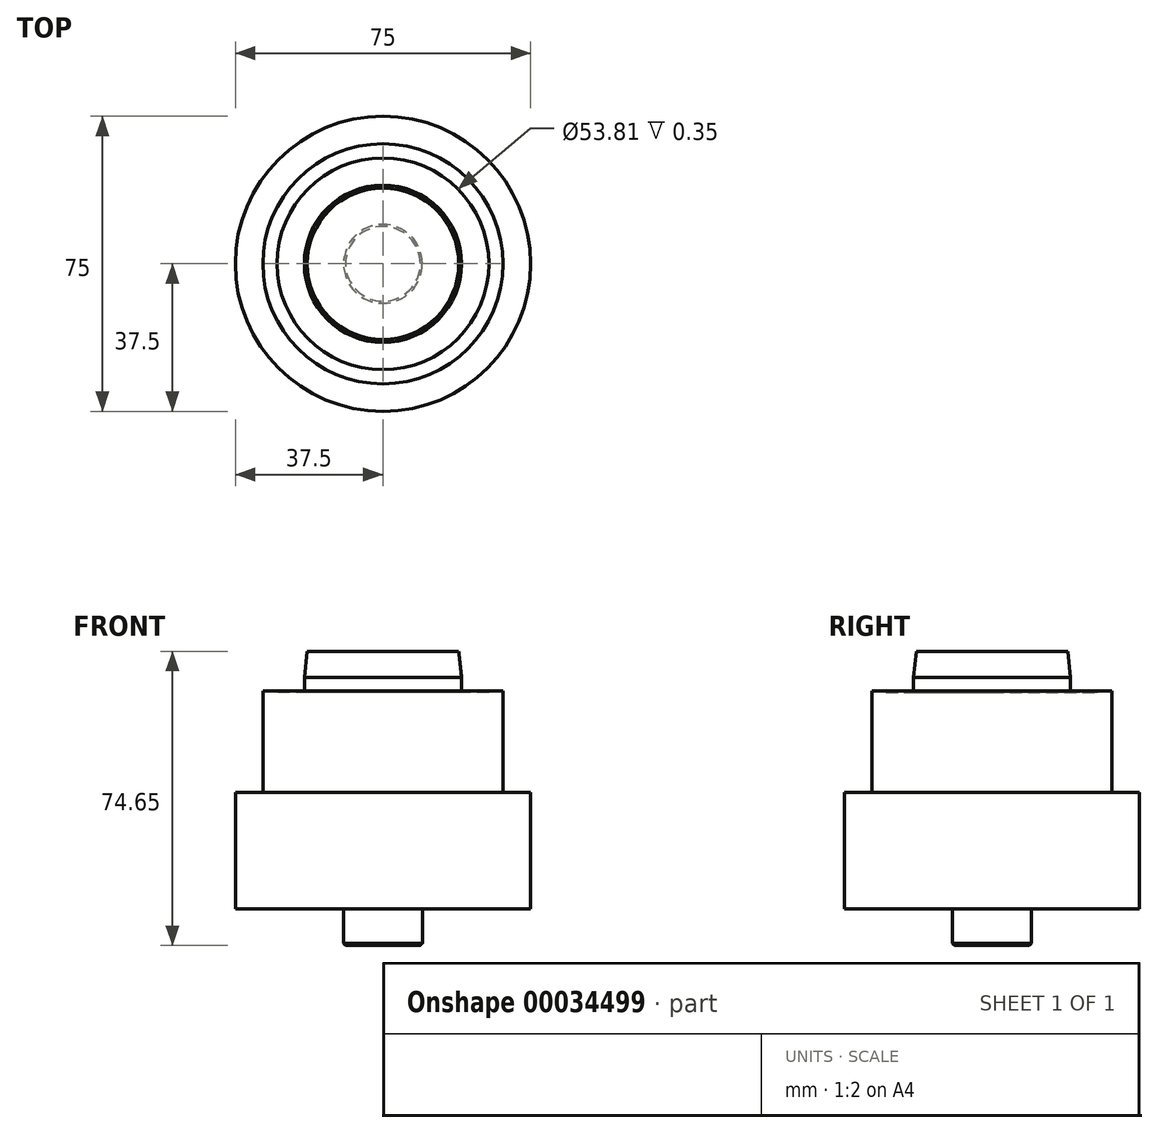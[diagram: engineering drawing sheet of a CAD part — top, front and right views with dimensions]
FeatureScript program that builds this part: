
annotation { "Feature Type Name" : "Feature", "Feature Type Description" : "" }
export const myFeature = defineFeature(function(context is Context, id is Id, definition is map)
    precondition{}
    {
        {
            var Q0;
            Q0=qCreatedBy(makeId("Front.planeOp"),FACE);
            var sketch = newSketch(context, id + "F0", { "sketchPlane" : qUnion([Q0])});
            skLineSegment(sketch, "E0", {"start": v(0, 93.75) * mm, "end": v(0, -3.98) * mm, "construction": true});
            skSolve(sketch);
        }
        {
            var Q0;
            Q0=qCreatedBy(makeId("Top.planeOp"),FACE);
            var sketch = newSketch(context, id + "F1", { "sketchPlane" : qUnion([Q0])});
            skCircle(sketch, "E1", {"center": v(0, 0) * mm, "radius": 10 * mm});
            skSolve(sketch);
        }
        {
            var Q0;
            Q0 = qSketchRegion(id + "F1", true);
            extrude(context, id + "F2", {"entities" : qUnion([Q0]), "depth" : 9.2 * mm});
        }
        {
            var Q0;
            Q0=makeQuery(id+"F2.opExtrude","CAP_FACE",FACE,{"disambiguationData":[OSD([sQuery(id+"F1.wireOp",EDGE,"E1")])],"isStart":false});
            var sketch = newSketch(context, id + "F3", { "sketchPlane" : qUnion([Q0])});
            skCircle(sketch, "E2", {"center": v(0, 0) * mm, "radius": 37.5 * mm});
            skSolve(sketch);
        }
        {
            var Q0;
            Q0 = qSketchRegion(id + "F3", true);
            extrude(context, id + "F4", {"entities" : qUnion([Q0]), "operationType" : NewBodyOperationType.ADD, "depth" : 29.6 * mm});
        }
        {
            var Q0;
            Q0=makeQuery(id+"F4.opExtrude","CAP_FACE",FACE,{"disambiguationData":[OSD([sQuery(id+"F3.wireOp",EDGE,"E2")])],"isStart":false});
            var sketch = newSketch(context, id + "F5", { "sketchPlane" : qUnion([Q0])});
            skCircle(sketch, "E3", {"center": v(0, 0) * mm, "radius": 30.5 * mm});
            skSolve(sketch);
        }
        {
            var Q0;
            Q0 = qSketchRegion(id + "F5", true);
            extrude(context, id + "F6", {"entities" : qUnion([Q0]), "operationType" : NewBodyOperationType.ADD, "depth" : 25.8 * mm});
        }
        {
            var Q0;
            Q0=makeQuery(id+"F6.opExtrude","CAP_FACE",FACE,{"disambiguationData":[OSD([sQuery(id+"F5.wireOp",EDGE,"E3")])],"isStart":false});
            var sketch = newSketch(context, id + "F7", { "sketchPlane" : qUnion([Q0])});
            skCircle(sketch, "E4", {"center": v(0, 0) * mm, "radius": 26.9 * mm});
            skSolve(sketch);
        }
        {
            var Q0;
            Q0 = qSketchRegion(id + "F7", true);
            extrude(context, id + "F8", {"entities" : qUnion([Q0]), "operationType" : NewBodyOperationType.REMOVE, "oppositeDirection" : true, "depth" : 0.35 * mm});
        }
        {
            var Q0;
            Q0=makeQuery(id+"F8.boolean.opBoolean","COPY",FACE,{"derivedFrom":makeQuery(id+"F8.opExtrude","CAP_FACE",FACE,{"disambiguationData":[OSD([sQuery(id+"F7.wireOp",EDGE,"E4")])],"isStart":false})});
            var sketch = newSketch(context, id + "F9", { "sketchPlane" : qUnion([Q0])});
            skLineSegment(sketch, "E5", {"start": v(0, 17.38) * mm, "end": v(0, -19.78) * mm, "construction": true});
            skSolve(sketch);
        }
        {
            var Q0;
            Q0=makeQuery(id+"F6UNSWDGwlZitm0_1.opRevolve","SWEPT_EDGE",EDGE,{"disambiguationData":[OSD([sQuery(id+"Fxo4OY0H7vpecpR_1.wireOp",EDGE,"9f0356d1-925e-4ddc-828d-e82d80c523e6.bottom"),sQuery(id+"Fxo4OY0H7vpecpR_1.wireOp",EDGE,"090784d4-c261-4ad9-9b5f-4208fe60787c")])]});
            var Q1;
            Q1=makeQuery(id+"F8.boolean.opBoolean","COPY",EDGE,{"derivedFrom":makeQuery(id+"F8.opExtrude","CAP_EDGE",EDGE,{"disambiguationData":[OSD([sQuery(id+"F7.wireOp",EDGE,"E4")])],"isStart":true})});
            var Q2;
            Q2=makeQuery(id+"F2.opExtrude","CAP_EDGE",EDGE,{"disambiguationData":[OSD([sQuery(id+"F1.wireOp",EDGE,"E1")])],"isStart":true});
            chamfer(context, id + "F10", {"entities" : qUnion([Q0, Q1, Q2]), "width" : 0.5 * mm, "tangentPropagation" : true});
        }
        {
            var Q0;
            Q0=qCreatedBy(makeId("Front.planeOp"),FACE);
            var sketch = newSketch(context, id + "F11", { "sketchPlane" : qUnion([Q0])});
            skLineSegment(sketch, "E6.bottom", {"start": v(0, 74.65) * mm, "end": v(-19.25, 74.65) * mm});
            skLineSegment(sketch, "E6.top", {"start": v(0, 64.25) * mm, "end": v(-19.98, 64.25) * mm});
            skLineSegment(sketch, "E6.left", {"start": v(0, 74.65) * mm, "end": v(0, 64.25) * mm});
            skLineSegment(sketch, "E6.right", {"start": v(-19.98, 68.05) * mm, "end": v(-19.98, 64.25) * mm});
            skLineSegment(sketch, "E7", {"start": v(-19.25, 74.65) * mm, "end": v(-19.98, 68.05) * mm});
            skSolve(sketch);
        }
        {
            var Q0;
            Q0 = qSketchRegion(id + "F11", true);
            var Q1;
            Q1=sQuery(id+"F0.wireOp",EDGE,"E0");
            revolve(context, id + "F12", {"operationType" : NewBodyOperationType.ADD, "entities" : qUnion([Q0]), "axis" : qUnion([Q1]), "revolveType" : RevolveType.FULL});
        }
    });
